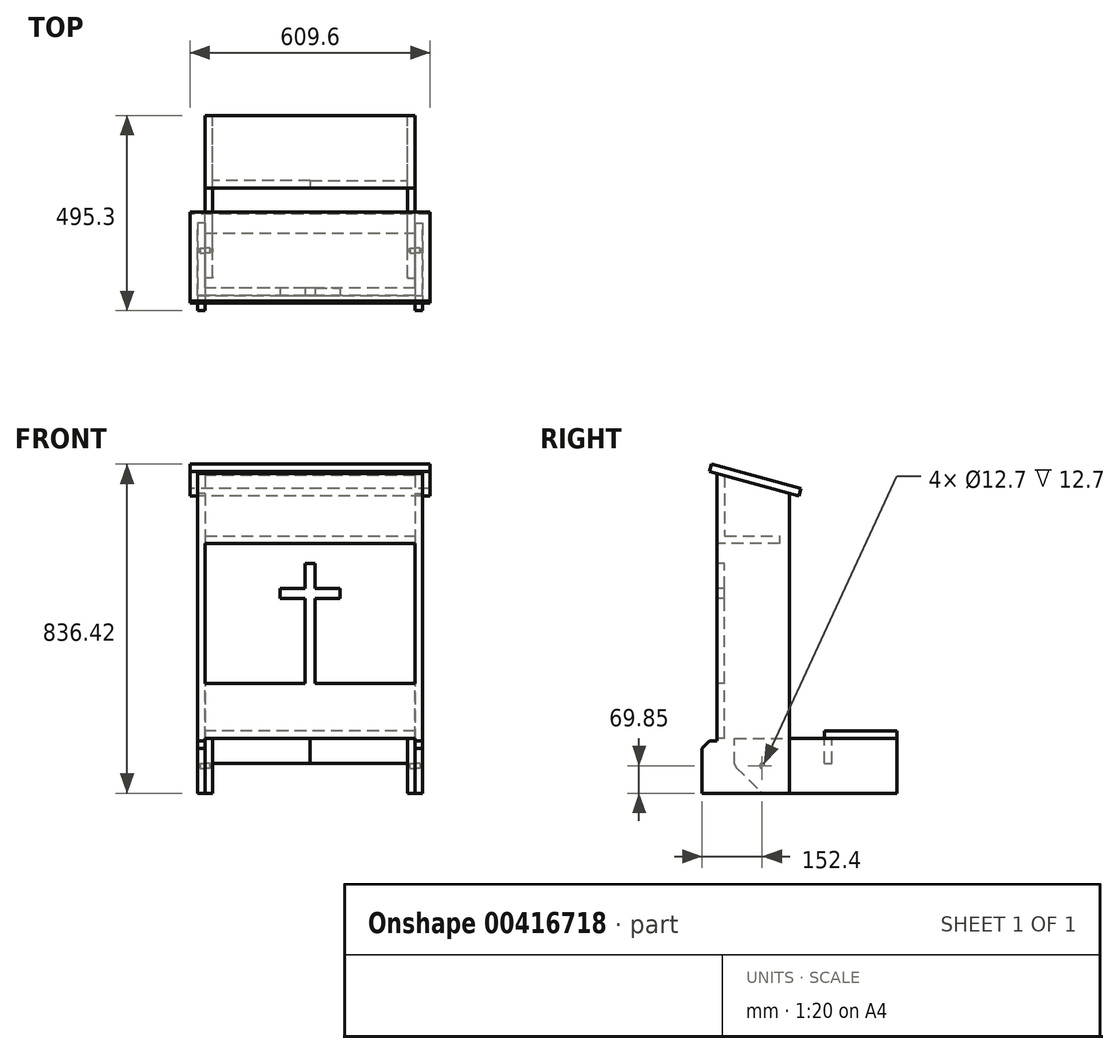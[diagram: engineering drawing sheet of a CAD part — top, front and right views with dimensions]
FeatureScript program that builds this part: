
annotation { "Feature Type Name" : "Feature", "Feature Type Description" : "" }
export const myFeature = defineFeature(function(context is Context, id is Id, definition is map)
    precondition{}
    {
        {
            var Q0;
            Q0=qCreatedBy(makeId("Front.planeOp"),FACE);
            var sketch = newSketch(context, id + "F0", { "sketchPlane" : qUnion([Q0])});
            skLineSegment(sketch, "E0", {"start": v(0, 0) * mm, "end": v(0, 865.52) * mm, "construction": true});
            skSolve(sketch);
        }
        {
            var Q0;
            Q0=qCreatedBy(makeId("Right.planeOp"),FACE);
            cPlane(context, id + "F1", {"entities" : qUnion([Q0]), "cplaneType" : CPlaneType.OFFSET, "offset" : 285.75 * mm, "width" : 152.4 * mm, "height" : 152.4 * mm});
        }
        {
            var Q0;
            Q0=qCreatedBy(id+"F1.planeOp",FACE);
            var sketch = newSketch(context, id + "F2", { "sketchPlane" : qUnion([Q0])});
            skLineSegment(sketch, "E1", {"start": v(0, 0) * mm, "end": v(-184.15, 0) * mm});
            skLineSegment(sketch, "E2", {"start": v(-184.15, 0) * mm, "end": v(-184.15, 812.8) * mm});
            skLineSegment(sketch, "E3", {"start": v(-184.15, 812.8) * mm, "end": v(0, 762) * mm});
            skLineSegment(sketch, "E4", {"start": v(0, 762) * mm, "end": v(0, 0) * mm});
            skSolve(sketch);
        }
        {
            var Q0;
            Q0=makeQuery(id+"F2.imprint","IMPRINT",FACE,{"disambiguationData":[TD([[makeQuery(id+"F2.imprint","IMPRINT",EDGE,{"derivedFrom":sQuery(id+"F2.wireOp",EDGE,"E1")}),-1.0]])]});
            extrude(context, id + "F3", {"entities" : qUnion([Q0]), "oppositeDirection" : true, "depth" : 19.05 * mm});
        }
        {
            var Q0;
            Q0=qCreatedBy(makeId("Right.planeOp"),FACE);
            var sketch = newSketch(context, id + "F4", { "sketchPlane" : qUnion([Q0])});
            skLineSegment(sketch, "E5", {"start": v(-198.13, 836.42) * mm, "end": v(-203.2, 818.06) * mm});
            skLineSegment(sketch, "E6", {"start": v(-203.2, 818.06) * mm, "end": v(23.3, 755.58) * mm});
            skLineSegment(sketch, "E7", {"start": v(23.3, 755.58) * mm, "end": v(28.36, 773.94) * mm});
            skLineSegment(sketch, "E8", {"start": v(28.36, 773.94) * mm, "end": v(-198.13, 836.42) * mm});
            skSolve(sketch);
        }
        {
            var Q0;
            Q0 = qSketchRegion(id + "F4", true);
            extrude(context, id + "F5", {"entities" : qUnion([Q0]), "depth" : 304.8 * mm});
        }
        {
            var Q0;
            Q0=makeQuery(id+"F3.opExtrude","SWEPT_FACE",FACE,{"disambiguationData":[OSD([sQuery(id+"F2.wireOp",EDGE,"E2")])]});
            var sketch = newSketch(context, id + "F6", { "sketchPlane" : qUnion([Q0])});
            skLineSegment(sketch, "E9", {"start": v(0, 139.7) * mm, "end": v(266.7, 139.7) * mm});
            skLineSegment(sketch, "E10", {"start": v(266.7, 139.7) * mm, "end": v(266.7, 279.4) * mm});
            skLineSegment(sketch, "E11", {"start": v(266.7, 279.4) * mm, "end": v(0, 279.4) * mm});
            skLineSegment(sketch, "E12", {"start": v(0, 279.4) * mm, "end": v(0, 139.7) * mm});
            skSolve(sketch);
        }
        {
            var Q0;
            Q0 = qSketchRegion(id + "F6", true);
            extrude(context, id + "F7", {"entities" : qUnion([Q0]), "oppositeDirection" : true, "depth" : 19.05 * mm});
        }
        {
            var Q0;
            Q0=qCreatedBy(makeId("Right.planeOp"),FACE);
            var sketch = newSketch(context, id + "F8", { "sketchPlane" : qUnion([Q0])});
            skLineSegment(sketch, "E13", {"start": v(-184.15, 812.8) * mm, "end": v(-165.1, 807.54) * mm});
            skLineSegment(sketch, "E14", {"start": v(-165.1, 807.54) * mm, "end": v(-165.1, 635) * mm});
            skLineSegment(sketch, "E15", {"start": v(-165.1, 635) * mm, "end": v(-184.15, 635) * mm});
            skLineSegment(sketch, "E16", {"start": v(-184.15, 635) * mm, "end": v(-184.15, 812.8) * mm});
            skSolve(sketch);
        }
        {
            var Q0;
            Q0 = qSketchRegion(id + "F8", true);
            var Q1;
            Q1=makeQuery(id+"F3.opExtrude","CAP_FACE",FACE,{"disambiguationData":[OSD([sQuery(id+"F2.wireOp",EDGE,"E1"),sQuery(id+"F2.wireOp",EDGE,"E2"),sQuery(id+"F2.wireOp",EDGE,"E3"),sQuery(id+"F2.wireOp",EDGE,"E4")])],"isStart":false});
            extrude(context, id + "F9", {"entities" : qUnion([Q0]), "endBound" : BoundingType.UP_TO_SURFACE, "endBoundEntityFace" : qUnion([Q1]), "depth" : 25.4 * mm});
        }
        {
            var Q0;
            Q0=makeQuery(id+"F3.opExtrude","CAP_FACE",FACE,{"disambiguationData":[OSD([sQuery(id+"F2.wireOp",EDGE,"E1"),sQuery(id+"F2.wireOp",EDGE,"E2"),sQuery(id+"F2.wireOp",EDGE,"E3"),sQuery(id+"F2.wireOp",EDGE,"E4")])],"isStart":false});
            var sketch = newSketch(context, id + "F10", { "sketchPlane" : qUnion([Q0])});
            skLineSegment(sketch, "E17.bottom", {"start": v(64.59, 0) * mm, "end": v(-273.05, 0) * mm});
            skLineSegment(sketch, "E17.top", {"start": v(139.7, 139.7) * mm, "end": v(-273.05, 139.7) * mm});
            skLineSegment(sketch, "E17.right", {"start": v(-273.05, 0) * mm, "end": v(-273.05, 139.7) * mm});
            skPoint(sketch, "E17.left.start.orphan", {"position": v(184.15, 0) * mm});
            skPoint(sketch, "E18.newPointA", {"position": v(92.08, 0) * mm});
            skLineSegment(sketch, "E19", {"start": v(69.85, 69.85) * mm, "end": v(139.7, 69.85) * mm, "construction": true});
            skLineSegment(sketch, "E20", {"start": v(69.85, 69.85) * mm, "end": v(69.85, 0) * mm, "construction": true});
            skLineSegment(sketch, "E21", {"start": v(135.98, 66.13) * mm, "end": v(73.57, 3.72) * mm});
            skPoint(sketch, "E22.visualSharp", {"position": v(139.7, 69.85) * mm});
            skArc(sketch, "E22.filletArc", {"start": v(135.98, 66.13) * mm, "mid": v(138.73, 70.25) * mm, "end": v(139.7, 75.11) * mm});
            skPoint(sketch, "E23.visualSharp", {"position": v(69.85, 0) * mm});
            skArc(sketch, "E23.filletArc", {"start": v(64.59, 0) * mm, "mid": v(69.45, 0.97) * mm, "end": v(73.57, 3.72) * mm});
            skLineSegment(sketch, "E24", {"start": v(139.7, 75.11) * mm, "end": v(139.7, 139.7) * mm});
            skSolve(sketch);
        }
        {
            var Q0;
            Q0 = qSketchRegion(id + "F10", true);
            extrude(context, id + "F11", {"entities" : qUnion([Q0]), "depth" : 19.05 * mm});
        }
        {
            var Q0;
            Q0=makeQuery(id+"F11.opExtrude","CAP_FACE",FACE,{"disambiguationData":[OSD([sQuery(id+"F10.wireOp",EDGE,"E17.bottom"),sQuery(id+"F10.wireOp",EDGE,"E17.top"),sQuery(id+"F10.wireOp",EDGE,"E17.right"),sQuery(id+"F10.wireOp",EDGE,"HSzywLzN-q3mH-uJCK-lopZ-LUy6DwC9F0fC")])],"isStart":true});
            var sketch = newSketch(context, id + "F12", { "sketchPlane" : qUnion([Q0])});
            skCircle(sketch, "E25", {"center": v(-69.85, 69.85) * mm, "radius": 6.35 * mm});
            skSolve(sketch);
        }
        {
            var Q0;
            Q0 = qSketchRegion(id + "F12", true);
            extrude(context, id + "F13", {"entities" : qUnion([Q0]), "operationType" : NewBodyOperationType.REMOVE, "oppositeDirection" : true, "depth" : 12.7 * mm});
        }
        {
            var Q0;
            Q0=makeQuery(id+"F3.opExtrude","CAP_FACE",FACE,{"disambiguationData":[OSD([sQuery(id+"F2.wireOp",EDGE,"E1"),sQuery(id+"F2.wireOp",EDGE,"E2"),sQuery(id+"F2.wireOp",EDGE,"E3"),sQuery(id+"F2.wireOp",EDGE,"E4")])],"isStart":false});
            var sketch = newSketch(context, id + "F14", { "sketchPlane" : qUnion([Q0])});
            skCircle(sketch, "E26.0", {"center": v(69.85, 69.85) * mm, "radius": 6.35 * mm});
            skSolve(sketch);
        }
        {
            var Q0;
            Q0 = qSketchRegion(id + "F14", true);
            extrude(context, id + "F15", {"entities" : qUnion([Q0]), "operationType" : NewBodyOperationType.REMOVE, "oppositeDirection" : true, "depth" : 12.7 * mm});
        }
        {
            var Q0;
            Q0=makeQuery(id+"F11.opExtrude","SWEPT_FACE",FACE,{"disambiguationData":[OSD([sQuery(id+"F10.wireOp",EDGE,"E17.top")])]});
            var sketch = newSketch(context, id + "F16", { "sketchPlane" : qUnion([Q0])});
            skLineSegment(sketch, "E27.bottom", {"start": v(266.7, 273.05) * mm, "end": v(0, 273.05) * mm});
            skLineSegment(sketch, "E27.top", {"start": v(266.7, 88.9) * mm, "end": v(0, 88.9) * mm});
            skLineSegment(sketch, "E27.left", {"start": v(266.7, 273.05) * mm, "end": v(266.7, 88.9) * mm});
            skLineSegment(sketch, "E27.right", {"start": v(0, 273.05) * mm, "end": v(0, 88.9) * mm});
            skSolve(sketch);
        }
        {
            var Q0;
            Q0 = qSketchRegion(id + "F16", true);
            extrude(context, id + "F17", {"entities" : qUnion([Q0]), "depth" : 19.05 * mm});
        }
        {
            var Q0;
            Q0=makeQuery(id+"F3.opExtrude","CAP_FACE",FACE,{"disambiguationData":[OSD([sQuery(id+"F2.wireOp",EDGE,"E1"),sQuery(id+"F2.wireOp",EDGE,"E2"),sQuery(id+"F2.wireOp",EDGE,"E3"),sQuery(id+"F2.wireOp",EDGE,"E4")])],"isStart":false});
            var sketch = newSketch(context, id + "F18", { "sketchPlane" : qUnion([Q0])});
            skLineSegment(sketch, "E28.bottom", {"start": v(165.1, 654.05) * mm, "end": v(25.4, 654.05) * mm});
            skLineSegment(sketch, "E28.top", {"start": v(165.1, 635) * mm, "end": v(25.4, 635) * mm});
            skLineSegment(sketch, "E28.left", {"start": v(165.1, 654.05) * mm, "end": v(165.1, 635) * mm});
            skLineSegment(sketch, "E29", {"start": v(25.4, 654.05) * mm, "end": v(25.4, 635) * mm});
            skSolve(sketch);
        }
        {
            var Q0;
            Q0 = qSketchRegion(id + "F18", true);
            var Q1;
            Q1=makeQuery(id+"F9.opExtrude","CAP_FACE",FACE,{"disambiguationData":[OSD([sQuery(id+"F8.wireOp",EDGE,"E13"),sQuery(id+"F8.wireOp",EDGE,"E14"),sQuery(id+"F8.wireOp",EDGE,"E15"),sQuery(id+"F8.wireOp",EDGE,"E16")])],"isStart":true});
            extrude(context, id + "F19", {"entities" : qUnion([Q0]), "endBound" : BoundingType.UP_TO_SURFACE, "endBoundEntityFace" : qUnion([Q1]), "depth" : 25.4 * mm});
        }
        {
            var Q0;
            Q0=makeQuery(id+"F7.opExtrude","CAP_FACE",FACE,{"disambiguationData":[OSD([sQuery(id+"F6.wireOp",EDGE,"E9"),sQuery(id+"F6.wireOp",EDGE,"E10"),sQuery(id+"F6.wireOp",EDGE,"E11"),sQuery(id+"F6.wireOp",EDGE,"E12")])],"isStart":true});
            var sketch = newSketch(context, id + "F20", { "sketchPlane" : qUnion([Q0])});
            skLineSegment(sketch, "E30", {"start": v(0, 279.4) * mm, "end": v(12.7, 279.4) * mm});
            skLineSegment(sketch, "E31", {"start": v(12.7, 279.4) * mm, "end": v(12.7, 495.3) * mm});
            skLineSegment(sketch, "E32", {"start": v(12.7, 495.3) * mm, "end": v(76.2, 495.3) * mm});
            skLineSegment(sketch, "E33", {"start": v(76.2, 495.3) * mm, "end": v(76.2, 520.7) * mm});
            skLineSegment(sketch, "E34", {"start": v(76.2, 520.7) * mm, "end": v(12.7, 520.7) * mm});
            skLineSegment(sketch, "E35", {"start": v(12.7, 520.7) * mm, "end": v(12.7, 584.2) * mm});
            skLineSegment(sketch, "E36", {"start": v(12.7, 584.2) * mm, "end": v(0, 584.2) * mm});
            skLineSegment(sketch, "E37", {"start": v(0, 584.2) * mm, "end": v(0, 279.4) * mm});
            skLineSegment(sketch, "E38", {"start": v(76.2, 508) * mm, "end": v(0, 508) * mm, "construction": true});
            skSolve(sketch);
        }
        {
            var Q0;
            Q0 = qSketchRegion(id + "F20", true);
            extrude(context, id + "F21", {"entities" : qUnion([Q0]), "oppositeDirection" : true, "depth" : 19.05 * mm});
        }
        {
            var Q0;
            Q0=makeQuery(id+"F3.opExtrude","CAP_FACE",FACE,{"disambiguationData":[OSD([sQuery(id+"F2.wireOp",EDGE,"E1"),sQuery(id+"F2.wireOp",EDGE,"E2"),sQuery(id+"F2.wireOp",EDGE,"E3"),sQuery(id+"F2.wireOp",EDGE,"E4")])],"isStart":true});
            var sketch = newSketch(context, id + "F22", { "sketchPlane" : qUnion([Q0])});
            skLineSegment(sketch, "E39", {"start": v(-184.15, 133.35) * mm, "end": v(-203.2, 133.35) * mm});
            skLineSegment(sketch, "E40", {"start": v(-203.2, 133.35) * mm, "end": v(-222.25, 114.3) * mm});
            skLineSegment(sketch, "E41", {"start": v(-222.25, 114.3) * mm, "end": v(-222.25, 0) * mm});
            skLineSegment(sketch, "E42", {"start": v(-222.25, 0) * mm, "end": v(-184.15, 0) * mm});
            skSolve(sketch);
        }
        {
            var Q0;
            {var subQ1=sQuery(id+"F22.wireOp",EDGE,"E39");Q0=makeQuery(id+"F22.imprint","IMPRINT",FACE,{"disambiguationData":[TD([[makeQuery(id+"F22.imprint","IMPRINT",EDGE,{"derivedFrom":subQ1}),1.0]])]});}
            extrude(context, id + "F23", {"entities" : qUnion([Q0]), "oppositeDirection" : true, "depth" : 19.05 * mm, "offsetDistance" : 25.4 * mm});
        }
        {
            var Q0;
            Q0=makeQuery(id+"F17.opExtrude","CAP_FACE",FACE,{"disambiguationData":[OSD([sQuery(id+"F16.wireOp",EDGE,"E27.bottom"),sQuery(id+"F16.wireOp",EDGE,"E27.top"),sQuery(id+"F16.wireOp",EDGE,"E27.left"),sQuery(id+"F16.wireOp",EDGE,"E27.right")])],"isStart":true});
            var sketch = newSketch(context, id + "F24", { "sketchPlane" : qUnion([Q0])});
            skLineSegment(sketch, "E43.bottom", {"start": v(0, -88.9) * mm, "end": v(247.65, -88.9) * mm});
            skLineSegment(sketch, "E43.top", {"start": v(0, -107.95) * mm, "end": v(247.65, -107.95) * mm});
            skLineSegment(sketch, "E43.left", {"start": v(0, -88.9) * mm, "end": v(0, -107.95) * mm});
            skLineSegment(sketch, "E43.right", {"start": v(247.65, -88.9) * mm, "end": v(247.65, -107.95) * mm});
            skSolve(sketch);
        }
        {
            var Q0;
            Q0 = qSketchRegion(id + "F24", true);
            extrude(context, id + "F25", {"entities" : qUnion([Q0]), "depth" : 63.5 * mm, "offsetDistance" : 25.4 * mm});
        }
        {
            var Q0;
            Q0=makeQuery(id+"F5.opExtrude","SWEPT_BODY",BODY,{"disambiguationData":[OSD([sQuery(id+"F4.wireOp",EDGE,"E5"),sQuery(id+"F4.wireOp",EDGE,"E6"),sQuery(id+"F4.wireOp",EDGE,"E7"),sQuery(id+"F4.wireOp",EDGE,"E8")])]});
            var Q1;
            Q1=makeQuery(id+"F7.opExtrude","SWEPT_BODY",BODY,{"disambiguationData":[OSD([sQuery(id+"F6.wireOp",EDGE,"E9"),sQuery(id+"F6.wireOp",EDGE,"E10"),sQuery(id+"F6.wireOp",EDGE,"E11"),sQuery(id+"F6.wireOp",EDGE,"E12")])]});
            var Q2;
            Q2=makeQuery(id+"F17.opExtrude","SWEPT_BODY",BODY,{"disambiguationData":[OSD([sQuery(id+"F16.wireOp",EDGE,"E27.bottom"),sQuery(id+"F16.wireOp",EDGE,"E27.top"),sQuery(id+"F16.wireOp",EDGE,"E27.left"),sQuery(id+"F16.wireOp",EDGE,"E27.right")])]});
            var Q3;
            Q3=qCreatedBy(makeId("Right.planeOp"),FACE);
            mirror(context, id + "F26", {"operationType" : NewBodyOperationType.ADD, "entities" : qUnion([Q0, Q1, Q2]), "mirrorPlane" : qUnion([Q3])});
        }
        {
            var Q0;
            Q0=makeQuery(id+"F3.opExtrude","SWEPT_BODY",BODY,{"disambiguationData":[OSD([sQuery(id+"F2.wireOp",EDGE,"E1"),sQuery(id+"F2.wireOp",EDGE,"E2"),sQuery(id+"F2.wireOp",EDGE,"E3"),sQuery(id+"F2.wireOp",EDGE,"E4")])]});
            var Q1;
            Q1=makeQuery(id+"F11.opExtrude","SWEPT_BODY",BODY,{"disambiguationData":[OSD([sQuery(id+"F10.wireOp",EDGE,"E17.bottom"),sQuery(id+"F10.wireOp",EDGE,"E17.top"),sQuery(id+"F10.wireOp",EDGE,"E17.left"),sQuery(id+"F10.wireOp",EDGE,"E17.right")])]});
            var Q2;
            Q2=makeQuery(id+"FpNn2GEh7o8HeF5_7.opExtrude","SWEPT_BODY",BODY,{"disambiguationData":[OSD([sQuery(id+"FFjgRWVul3OzuZO_7.wireOp",EDGE,"7a70f0ab-1529-4423-b222-b16315fa062a"),sQuery(id+"FFjgRWVul3OzuZO_7.wireOp",EDGE,"e83c5fb9-ba6c-45aa-8132-f22fb38a4e7c"),sQuery(id+"FFjgRWVul3OzuZO_7.wireOp",EDGE,"47cd6c8a-f438-4588-8dc6-d95de24094d0")])]});
            var Q3;
            Q3=qCreatedBy(makeId("Right.planeOp"),FACE);
            mirror(context, id + "F27", {"entities" : qUnion([Q0, Q1, Q2]), "mirrorPlane" : qUnion([Q3])});
        }
        {
            var Q0;
            Q0=makeQuery(id+"F21.opExtrude","SWEPT_BODY",BODY,{"disambiguationData":[OSD([sQuery(id+"F20.wireOp",EDGE,"E30"),sQuery(id+"F20.wireOp",EDGE,"E31"),sQuery(id+"F20.wireOp",EDGE,"E32"),sQuery(id+"F20.wireOp",EDGE,"E33"),sQuery(id+"F20.wireOp",EDGE,"E34"),sQuery(id+"F20.wireOp",EDGE,"E35"),sQuery(id+"F20.wireOp",EDGE,"E36"),sQuery(id+"F20.wireOp",EDGE,"E37")])]});
            var Q1;
            Q1=makeQuery(id+"F19.opExtrude","SWEPT_BODY",BODY,{"disambiguationData":[OSD([sQuery(id+"F18.wireOp",EDGE,"E28.bottom"),sQuery(id+"F18.wireOp",EDGE,"E28.top"),sQuery(id+"F18.wireOp",EDGE,"E28.left"),sQuery(id+"F18.wireOp",EDGE,"E28.right")])]});
            var Q2;
            Q2=qCreatedBy(makeId("Right.planeOp"),FACE);
            mirror(context, id + "F28", {"operationType" : NewBodyOperationType.ADD, "entities" : qUnion([Q0, Q1]), "mirrorPlane" : qUnion([Q2])});
        }
        {
            var Q0;
            Q0=makeQuery(id+"F9.opExtrude","SWEPT_BODY",BODY,{"disambiguationData":[OSD([sQuery(id+"F8.wireOp",EDGE,"E13"),sQuery(id+"F8.wireOp",EDGE,"E14"),sQuery(id+"F8.wireOp",EDGE,"E15"),sQuery(id+"F8.wireOp",EDGE,"E16")])]});
            var Q1;
            Q1=makeQuery(id+"F23.opExtrude","SWEPT_BODY",BODY,{"disambiguationData":[OSD([sQuery(id+"F2.wireOp",EDGE,"E2"),sQuery(id+"F22.wireOp",EDGE,"E39"),sQuery(id+"F22.wireOp",EDGE,"E40"),sQuery(id+"F22.wireOp",EDGE,"E41"),sQuery(id+"F22.wireOp",EDGE,"E42")])]});
            var Q2;
            Q2=makeQuery(id+"F25.opExtrude","SWEPT_BODY",BODY,{"disambiguationData":[OSD([sQuery(id+"F24.wireOp",EDGE,"E43.bottom"),sQuery(id+"F24.wireOp",EDGE,"E43.top"),sQuery(id+"F24.wireOp",EDGE,"E43.left"),sQuery(id+"F24.wireOp",EDGE,"E43.right")])]});
            var Q3;
            Q3=qCreatedBy(makeId("Right.planeOp"),FACE);
            mirror(context, id + "F29", {"operationType" : NewBodyOperationType.ADD, "entities" : qUnion([Q0, Q1, Q2]), "mirrorPlane" : qUnion([Q3])});
        }
    });
